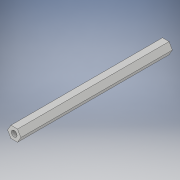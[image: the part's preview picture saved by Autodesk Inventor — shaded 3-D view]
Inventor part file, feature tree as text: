
AUTODESK INVENTOR PART (.ipt)
format: ipt  version: 2018 (Build 220112000, 112)  size: 100,864 bytes
history: native  units: in
note: dims shown in document units (in); Inventor stores cm internally (conversion verified against a paired STEP export)
features: extrude x2, sketch x2
ambient origin geometry x8: Origin, YZ Plane, XZ Plane, XY Plane, X Axis, Y Axis, Z Axis, Center Point
bodies: Solid1 (feature_tree)
feature tree (4):
  extrude  "Extrusion1"  Depth=6.625in TaperAngle=0.0deg
  extrude  "Extrusion2"  Depth=8.0in TaperAngle=0.0deg
  sketch  "Sketch1"  dims[d0=0.5in d1=6.625in d2=0.0in]
  sketch  "Sketch2"  dims[d3=0.25in d4=8.0in d5=0.0in]
